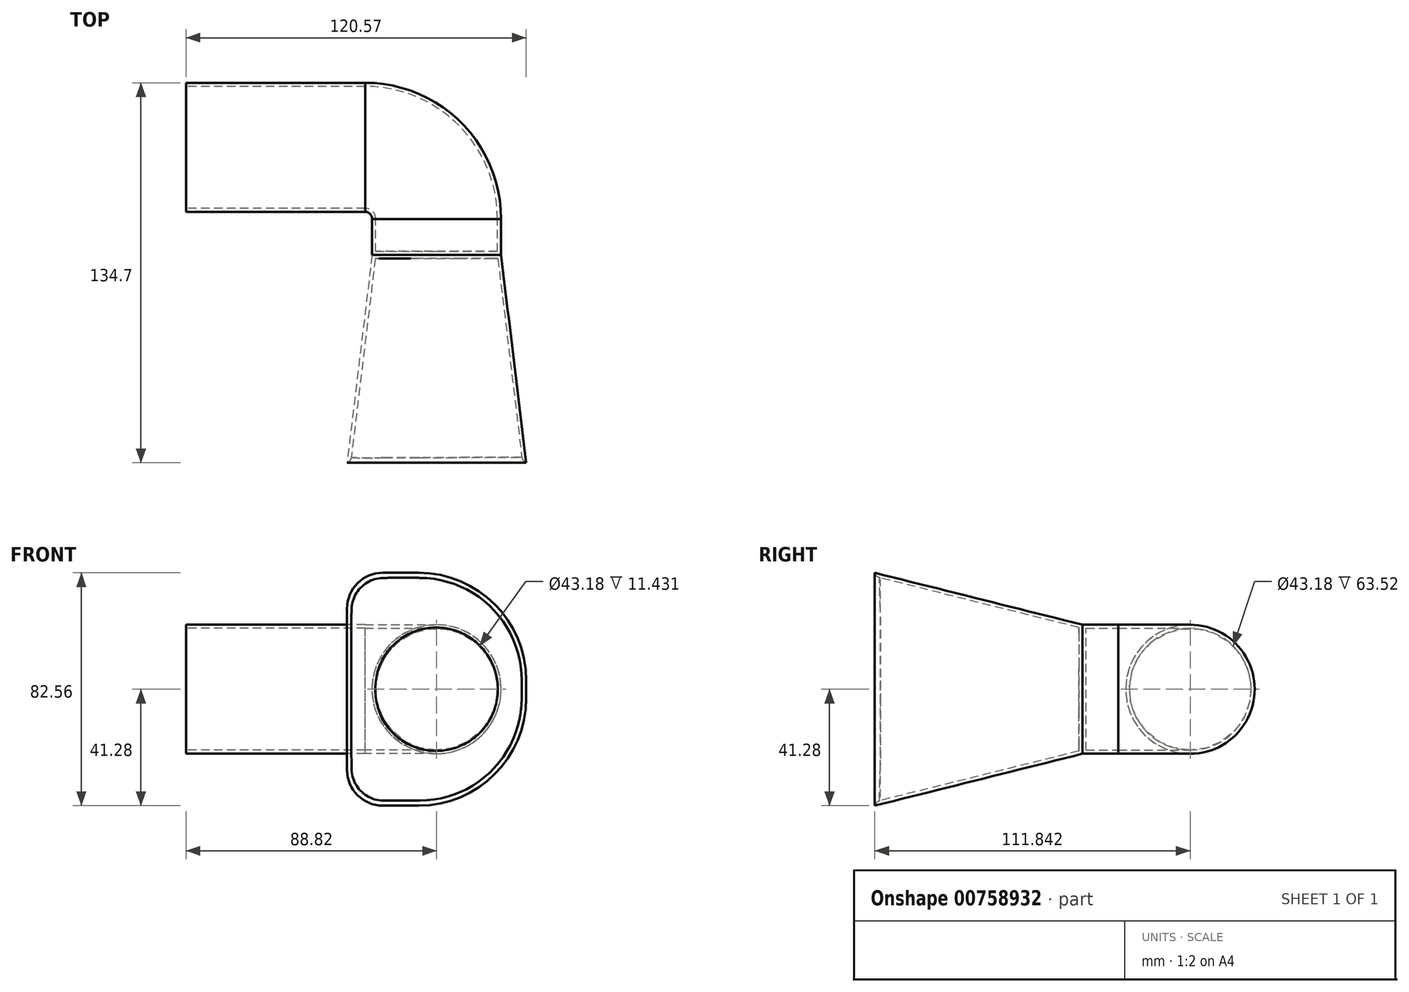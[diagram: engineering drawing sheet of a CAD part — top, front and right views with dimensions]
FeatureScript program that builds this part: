
annotation { "Feature Type Name" : "Feature", "Feature Type Description" : "" }
export const myFeature = defineFeature(function(context is Context, id is Id, definition is map)
    precondition{}
    {
        {
            var Q0;
            Q0=qCreatedBy(makeId("Front.planeOp"),FACE);
            cPlane(context, id + "F0", {"entities" : qUnion([Q0]), "cplaneType" : CPlaneType.OFFSET, "offset" : 73.66 * mm, "oppositeDirection" : true, "width" : 152.4 * mm, "height" : 152.4 * mm});
        }
        {
            var Q0;
            Q0=qCreatedBy(id+"F0.planeOp",FACE);
            var sketch = newSketch(context, id + "F1", { "sketchPlane" : qUnion([Q0])});
            skCircle(sketch, "E0", {"center": v(0, 0) * mm, "radius": 22.86 * mm});
            skSolve(sketch);
        }
        {
            var Q0;
            Q0=qCreatedBy(makeId("Right.planeOp"),FACE);
            var sketch = newSketch(context, id + "F2", { "sketchPlane" : qUnion([Q0])});
            skLineSegment(sketch, "E1", {"start": v(0, 0) * mm, "end": v(73.74, 0) * mm});
            skSolve(sketch);
        }
        {
            var Q0;
            Q0=qCreatedBy(makeId("Front.planeOp"),FACE);
            var sketch = newSketch(context, id + "F3", { "sketchPlane" : qUnion([Q0])});
            skLineSegment(sketch, "E2.bottom", {"start": v(-19.05, 41.28) * mm, "end": v(-6.35, 41.28) * mm});
            skLineSegment(sketch, "E2.top", {"start": v(-19.05, -41.27) * mm, "end": v(-6.35, -41.27) * mm});
            skLineSegment(sketch, "E2.left", {"start": v(-31.75, 28.58) * mm, "end": v(-31.75, -28.58) * mm});
            skLineSegment(sketch, "E2.right", {"start": v(31.75, 3.18) * mm, "end": v(31.75, -3.18) * mm});
            skPoint(sketch, "E3.visualSharp", {"position": v(-31.75, 41.28) * mm});
            skArc(sketch, "E3.filletArc", {"start": v(-19.05, 41.28) * mm, "mid": v(-28.03, 37.56) * mm, "end": v(-31.75, 28.58) * mm});
            skPoint(sketch, "E4.visualSharp", {"position": v(-31.75, -41.27) * mm});
            skArc(sketch, "E4.filletArc", {"start": v(-31.75, -28.58) * mm, "mid": v(-28.03, -37.56) * mm, "end": v(-19.05, -41.28) * mm});
            skPoint(sketch, "E5.visualSharp", {"position": v(31.75, -41.27) * mm});
            skArc(sketch, "E5.filletArc", {"start": v(-6.35, -41.28) * mm, "mid": v(20.6, -30.12) * mm, "end": v(31.75, -3.18) * mm});
            skPoint(sketch, "E6.visualSharp", {"position": v(31.75, 41.28) * mm});
            skArc(sketch, "E6.filletArc", {"start": v(31.75, 3.18) * mm, "mid": v(20.6, 30.12) * mm, "end": v(-6.35, 41.28) * mm});
            skSolve(sketch);
        }
        {
            var Q0;
            Q0=makeQuery(id+"F3.imprint","IMPRINT",FACE,{"disambiguationData":[TD([[makeQuery(id+"F3.imprint","IMPRINT",EDGE,{"derivedFrom":sQuery(id+"F3.wireOp",EDGE,"E2.bottom")}),-1.0]])]});
            var Q1;
            Q1=makeQuery(id+"F1.imprint","IMPRINT",FACE,{"disambiguationData":[TD([[makeQuery(id+"F1.imprint","IMPRINT",EDGE,{"derivedFrom":sQuery(id+"F1.wireOp",EDGE,"E0")}),1.0]])]});
            loft(context, id + "F4", {"sheetProfilesArray" : [{ "sheetProfileEntities" : qUnion([Q0]) }, { "sheetProfileEntities" : qUnion([Q1]) }]});
        }
        {
            var Q0;
            Q0=qCreatedBy(makeId("Top.planeOp"),FACE);
            var sketch = newSketch(context, id + "F5", { "sketchPlane" : qUnion([Q0])});
            skLineSegment(sketch, "E7", {"start": v(0, 73.74) * mm, "end": v(0, 86.44) * mm});
            skLineSegment(sketch, "E8", {"start": v(-25.4, 111.84) * mm, "end": v(-88.9, 111.84) * mm});
            skPoint(sketch, "E9.visualSharp", {"position": v(0, 111.84) * mm});
            skArc(sketch, "E9.filletArc", {"start": v(0, 86.44) * mm, "mid": v(-7.44, 104.4) * mm, "end": v(-25.4, 111.84) * mm});
            skSolve(sketch);
        }
        {
            var Q0;
            Q0=qCreatedBy(makeId("Right.planeOp"),FACE);
            cPlane(context, id + "F6", {"entities" : qUnion([Q0]), "cplaneType" : CPlaneType.OFFSET, "offset" : 88.9 * mm, "oppositeDirection" : true, "width" : 152.4 * mm, "height" : 152.4 * mm});
        }
        {
            var Q0;
            Q0=makeQuery(id+"F1.imprint","IMPRINT",FACE,{"disambiguationData":[TD([[makeQuery(id+"F1.imprint","IMPRINT",EDGE,{"derivedFrom":sQuery(id+"F1.wireOp",EDGE,"E0")}),1.0]])]});
            var Q1;
            Q1=sQuery(id+"F5.wireOp",EDGE,"E8");
            var Q2;
            Q2=sQuery(id+"F5.wireOp",EDGE,"E9.filletArc");
            var Q3;
            Q3=sQuery(id+"F5.wireOp",EDGE,"E7");
            sweep(context, id + "F7", {"profiles" : qUnion([Q0]), "path" : qUnion([Q1, Q2, Q3])});
        }
        {
            var Q0;
            Q0=makeQuery(id+"F7.opSweep","CAP_FACE",FACE,{"disambiguationData":[OSD([sQuery(id+"F1.wireOp",EDGE,"E0"),sQuery(id+"F5.wireOp",VERTEX,"E8.end")])],"isStart":false});
            var Q1;
            Q1=makeQuery(id+"F4.opLoft","CAP_FACE",FACE,{"disambiguationData":[OSD([makeQuery(id+"F3.imprint","IMPRINT",FACE,{"disambiguationData":[TD([[makeQuery(id+"F3.imprint","IMPRINT",EDGE,{"derivedFrom":sQuery(id+"F3.wireOp",EDGE,"E2.bottom")}),-1.0]])]})])],"isStart":true});
            shell(context, id + "F8", {"entities" : qUnion([Q0, Q1]), "thickness" : 1.27 * mm});
        }
        {
            var Q0;
            Q0=makeQuery(id+"F8.opShell","OFFSET_EDGE",EDGE,{"disambiguationData":[OSD([sQuery(id+"F3.wireOp",EDGE,"E2.bottom"),sQuery(id+"F3.wireOp",EDGE,"E2.top"),sQuery(id+"F3.wireOp",EDGE,"E2.left"),sQuery(id+"F3.wireOp",EDGE,"E2.right"),sQuery(id+"F3.wireOp",EDGE,"E3.filletArc"),sQuery(id+"F3.wireOp",EDGE,"E4.filletArc"),sQuery(id+"F3.wireOp",EDGE,"E5.filletArc"),sQuery(id+"F3.wireOp",EDGE,"E6.filletArc")])]});
            fillet(context, id + "F9", {"entities" : qUnion([Q0]), "radius" : 2.54 * mm, "tangentPropagation" : true, "allowEdgeOverflow" : false});
        }
    });
